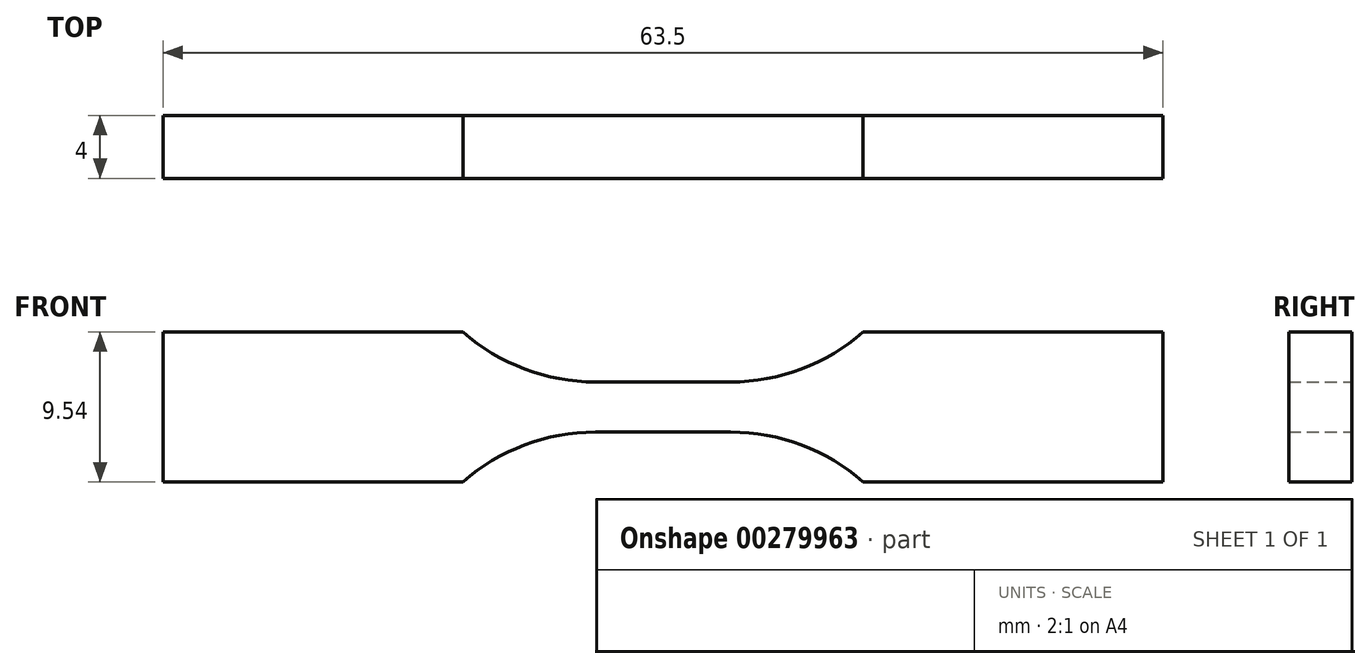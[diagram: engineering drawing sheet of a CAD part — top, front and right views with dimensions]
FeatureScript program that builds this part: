
annotation { "Feature Type Name" : "Feature", "Feature Type Description" : "" }
export const myFeature = defineFeature(function(context is Context, id is Id, definition is map)
    precondition{}
    {
        {
            var Q0;
            Q0=qCreatedBy(makeId("Front.planeOp"),FACE);
            var sketch = newSketch(context, id + "F0", { "sketchPlane" : qUnion([Q0])});
            skLineSegment(sketch, "E0", {"start": v(0, 1.6) * mm, "end": v(4.3, 1.6) * mm});
            skArc(sketch, "E1", {"start": v(4.3, 1.59) * mm, "mid": v(8.79, 2.41) * mm, "end": v(12.7, 4.76) * mm});
            skLineSegment(sketch, "E2", {"start": v(12.7, 4.77) * mm, "end": v(31.75, 4.77) * mm});
            skLineSegment(sketch, "E3", {"start": v(31.75, 4.77) * mm, "end": v(31.75, 0) * mm});
            skArc(sketch, "E4.MirrorCS", {"start": v(4.3, -1.59) * mm, "mid": v(8.79, -2.41) * mm, "end": v(12.7, -4.76) * mm});
            skLineSegment(sketch, "E5.MirrorCS", {"start": v(0, -1.6) * mm, "end": v(4.3, -1.6) * mm});
            skLineSegment(sketch, "E6.MirrorCS", {"start": v(31.75, -4.77) * mm, "end": v(31.75, 0) * mm});
            skLineSegment(sketch, "E7.MirrorCS", {"start": v(12.7, -4.77) * mm, "end": v(31.75, -4.77) * mm});
            skArc(sketch, "E8.MirrorCS", {"start": v(-4.3, 1.59) * mm, "mid": v(-8.79, 2.41) * mm, "end": v(-12.7, 4.76) * mm});
            skArc(sketch, "E9.MirrorCS", {"start": v(-4.3, -1.59) * mm, "mid": v(-8.79, -2.41) * mm, "end": v(-12.7, -4.76) * mm});
            skLineSegment(sketch, "E10.MirrorCS", {"start": v(-12.7, -4.76) * mm, "end": v(-31.75, -4.77) * mm});
            skLineSegment(sketch, "E11.MirrorCS", {"start": v(-31.75, -4.77) * mm, "end": v(-31.75, 0) * mm});
            skLineSegment(sketch, "E12.MirrorCS", {"start": v(-12.7, 4.77) * mm, "end": v(-31.75, 4.77) * mm});
            skLineSegment(sketch, "E13.MirrorCS", {"start": v(0, -1.59) * mm, "end": v(-4.3, -1.59) * mm});
            skLineSegment(sketch, "E14.MirrorCS", {"start": v(-31.75, 4.77) * mm, "end": v(-31.75, 0) * mm});
            skLineSegment(sketch, "E15.MirrorCS", {"start": v(0, 1.6) * mm, "end": v(-4.3, 1.6) * mm});
            skSolve(sketch);
        }
        {
            var Q0;
            Q0=makeQuery(id+"F0.imprint","IMPRINT",FACE,{"disambiguationData":[TD([[makeQuery(id+"F0.imprint","IMPRINT",EDGE,{"derivedFrom":sQuery(id+"F0.wireOp",EDGE,"E0")}),-1.0]])]});
            extrude(context, id + "F1", {"entities" : qUnion([Q0]), "endBound" : BoundingType.SYMMETRIC, "depth" : 4 * mm});
        }
    });
